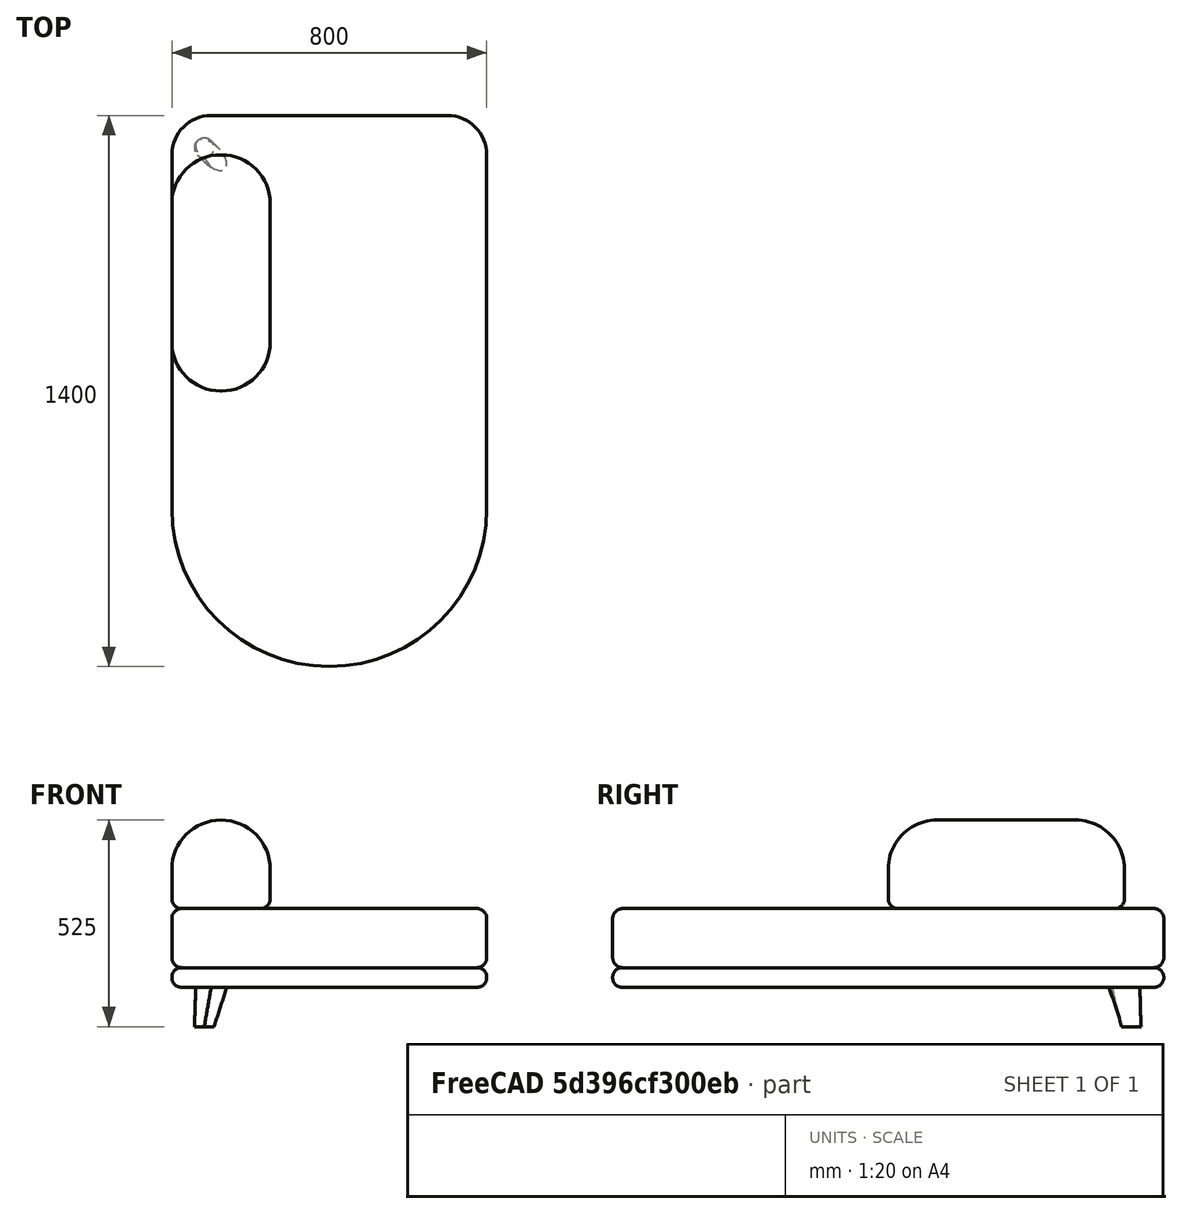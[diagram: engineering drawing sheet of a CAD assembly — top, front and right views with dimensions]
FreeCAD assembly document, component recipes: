
FREECAD ASSEMBLY — COMPONENT RECIPES ("Drawing room Sofa lounger")

This assembly document has 7 components, labeled P0..P6 below (a component is one placed body or linked part). 7 of them carry a construction recipe — the FreeCAD feature program that regenerates the part from scratch, quoted from this document or its linked companion documents; the rest are supplied as boundary geometry only. No exploded tour is included for this assembly.
COMPONENT P0 — recipe-attached ("Backrest001", modeled in this document).
Construction recipe (the document's own serialized feature program — sketch geometry with constraints, then the solid features built on it; lengths are millimeters unless a unit is written):

FEATURE [Sketcher::SketchObject] Sketch002
  ArcFitTolerance = 1e-06
  AttachmentSupport = -> [XZ_Plane002]
  FullyConstrained = true
  MakeInternals = false
  MapMode = 5
  Placement = pos=(0,0,0) rot=(1,0,0;1.5708rad)
  sketch-geometry (5):
    g0: LineSegment StartX=0 StartY=0 StartZ=0 EndX=250 EndY=0 EndZ=0
    g1: LineSegment StartX=250 StartY=0 StartZ=0 EndX=250 EndY=100 EndZ=0
    g2: LineSegment [constr] StartX=250 StartY=100 StartZ=0 EndX=0 EndY=100 EndZ=0
    g3: LineSegment StartX=0 StartY=100 StartZ=0 EndX=0 EndY=0 EndZ=0
    g4: ArcOfCircle CenterX=125 CenterY=100 CenterZ=0 NormalX=0 NormalY=0 NormalZ=1 AngleXU=0 Radius=125 StartAngle=0 EndAngle=3.14159
  constraints (14):
    c: Coincident(g0,g1)
    c: Coincident(g1,g2)
    c: Coincident(g2,g3)
    c: Coincident(g3,g0)
    c: Horizontal(g0)
    c: Horizontal(g2)
    c: Vertical(g1)
    c: Vertical(g3)
    c: Distance(g1,g3) = 250
    c: Distance(g0,g2) = 100
    c: Coincident(g0,g-1)
    c: Coincident(g4,g2)
    c: Coincident(g4,g1)
    c: PointOnObject(g4,g2)
FEATURE [PartDesign::Pad] Pad002
  Direction = (0,-1,2e-16)
  Length = 600
  Length2 = 10
  Placement = pos=(0,0,0) rot=(1,0,0;1.5708rad)
  Profile = -> Sketch002
  ReferenceAxis = -> Sketch002 [N_Axis]
  Refine = true
  Suppressed = false
  Type = 0
FEATURE [PartDesign::Fillet] Fillet002
  Base = -> Pad002 [Edge9,Edge10]
  BaseFeature = -> Pad002
  Placement = pos=(0,0,0) rot=(1,0,0;1.5708rad)
  Radius = 124
  Refine = true
  SupportTransform = false
  Suppressed = false
  UseAllEdges = false
FEATURE [PartDesign::Fillet] Fillet003
  Base = -> Fillet002 [Face1]
  BaseFeature = -> Fillet002
  Placement = pos=(0,0,0) rot=(1,0,0;1.5708rad)
  Radius = 25
  Refine = true
  SupportTransform = false
  Suppressed = false
  UseAllEdges = true
FEATURE [PartDesign::Body] Body002  label="Backrest"
  AllowCompound = false
  Group = -> [Sketch002,Pad002,Fillet002,Fillet003]
  Origin = -> Origin002
  Placement = pos=(0,-100,200) rot=(0,0,1;0rad)
  Tip = -> Fillet003
COMPONENT P1 — recipe-attached ("Base001", modeled in this document).
Construction recipe (the document's own serialized feature program — sketch geometry with constraints, then the solid features built on it; lengths are millimeters unless a unit is written):

FEATURE [Sketcher::SketchObject] Sketch
  ArcFitTolerance = 1e-06
  AttachmentSupport = -> [XY_Plane]
  FullyConstrained = true
  MakeInternals = false
  MapMode = 5
  sketch-geometry (6):
    g0: LineSegment StartX=100 StartY=0 StartZ=0 EndX=700 EndY=0 EndZ=0
    g1: ArcOfCircle CenterX=700 CenterY=-100 CenterZ=0 NormalX=0 NormalY=0 NormalZ=1 AngleXU=0 Radius=100 StartAngle=1e-16 EndAngle=1.5708
    g2: LineSegment StartX=800 StartY=-100 StartZ=0 EndX=800 EndY=-1000 EndZ=0
    g3: ArcOfCircle CenterX=400 CenterY=-1000 CenterZ=0 NormalX=0 NormalY=0 NormalZ=1 AngleXU=0 Radius=400 StartAngle=3.14159 EndAngle=6.28319
    g4: LineSegment StartX=0 StartY=-1000 StartZ=0 EndX=0 EndY=-100 EndZ=0
    g5: ArcOfCircle CenterX=100 CenterY=-100 CenterZ=0 NormalX=0 NormalY=0 NormalZ=1 AngleXU=0 Radius=100 StartAngle=1.5708 EndAngle=3.14159
  constraints (15):
    c: PointOnObject(g0,g-1)
    c: Horizontal(g0)
    c: Tangent(g0,g1) = 1.5708
    c: Tangent(g1,g2) = 1.5708
    c: Tangent(g2,g3) = 1.5708
    c: PointOnObject(g3,g-2)
    c: Tangent(g3,g4) = 1.5708
    c: Tangent(g4,g5) = 1.5708
    c: Radius(g1) = 100
    c: Radius(g5) = 100
    c: Vertical(g4)
    c: Vertical(g2)
    c: Tangent(g5,g0) = 1.5708
    c: DistanceX(g0,g0) = 600
    c: DistanceY(g2,g2) = 900
FEATURE [PartDesign::Pad] Pad
  Direction = (0,0,1)
  Length = 50
  Length2 = 10
  Profile = -> Sketch
  ReferenceAxis = -> Sketch [N_Axis]
  Refine = true
  Suppressed = false
  Type = 0
FEATURE [PartDesign::Fillet] Fillet001
  Base = -> Pad [?Face10]
  BaseFeature = -> Pad
  Radius = 24
  Refine = true
  SupportTransform = false
  Suppressed = false
  UseAllEdges = true
FEATURE [PartDesign::Body] Body  label="Base"
  AllowCompound = false
  Group = -> [Sketch,Pad,Fillet001]
  Origin = -> Origin
  Tip = -> Fillet001
COMPONENT P2 — recipe-attached ("Cushion001", modeled in this document).
Construction recipe (the document's own serialized feature program — sketch geometry with constraints, then the solid features built on it; lengths are millimeters unless a unit is written):

FEATURE [Sketcher::SketchObject] Sketch001
  ArcFitTolerance = 1e-06
  AttachmentSupport = -> [XY_Plane001]
  FullyConstrained = true
  MakeInternals = false
  MapMode = 5
  sketch-geometry (7):
    g0: LineSegment StartX=0 StartY=-100 StartZ=0 EndX=0 EndY=-1000 EndZ=0
    g1: LineSegment StartX=800 StartY=-1000 StartZ=0 EndX=800 EndY=-100 EndZ=0
    g2: LineSegment StartX=700 StartY=0 StartZ=0 EndX=100 EndY=0 EndZ=0
    g3: ArcOfCircle CenterX=100 CenterY=-100 CenterZ=0 NormalX=0 NormalY=0 NormalZ=1 AngleXU=0 Radius=100 StartAngle=1.5708 EndAngle=3.14159
    g4: ArcOfCircle CenterX=700 CenterY=-100 CenterZ=0 NormalX=0 NormalY=0 NormalZ=1 AngleXU=0 Radius=100 StartAngle=0 EndAngle=1.5708
    g5: GeomPoint [constr] X=0 Y=0 Z=0
    g6: ArcOfCircle CenterX=400 CenterY=-1000 CenterZ=0 NormalX=0 NormalY=0 NormalZ=1 AngleXU=0 Radius=400 StartAngle=3.14159 EndAngle=6.28319
  constraints (16):
    c: Tangent(g0,g3) = -1.5708
    c: Tangent(g1,g4) = -1.5708
    c: Tangent(g2,g4) = -1.5708
    c: Tangent(g2,g3) = -1.5708
    c: Vertical(g0)
    c: Vertical(g1)
    c: Horizontal(g2)
    c: PointOnObject(g5,g0)
    c: PointOnObject(g5,g2)
    c: Distance(g0,g1) = 800
    c: Coincident(g5,g-1)
    c: Tangent(g6,g1) = -1.5708
    c: Tangent(g6,g0) = -1.5708
    c: Radius(g4) = 100
    c: Radius(g3) = 100
    c: Distance(g1) = 900
FEATURE [PartDesign::Pad] Pad001
  Direction = (0,0,1)
  Length = 150
  Length2 = 10
  Profile = -> Sketch001
  ReferenceAxis = -> Sketch001 [N_Axis]
  Refine = true
  Suppressed = false
  Type = 0
FEATURE [PartDesign::Fillet] Fillet
  Base = -> Pad001
  BaseFeature = -> Pad001
  Radius = 25
  Refine = true
  SupportTransform = false
  Suppressed = false
  UseAllEdges = true
FEATURE [PartDesign::Body] Body001  label="Cushion"
  AllowCompound = false
  Group = -> [Sketch001,Pad001,Fillet]
  Origin = -> Origin001
  Placement = pos=(0,0,50) rot=(0,0,1;0rad)
  Tip = -> Fillet
COMPONENT P3 — recipe-attached ("Legs001", modeled in this document).
Construction recipe (the document's own serialized feature program — sketch geometry with constraints, then the solid features built on it; lengths are millimeters unless a unit is written):

FEATURE [Sketcher::SketchObject] Sketch003
  ArcFitTolerance = 1e-06
  AttachmentSupport = -> [XY_Plane003]
  FullyConstrained = true
  MakeInternals = false
  MapMode = 5
  sketch-geometry (5):
    g0: Ellipse CenterX=0 CenterY=0 CenterZ=0 NormalX=0 NormalY=0 NormalZ=1 MajorRadius=50 MinorRadius=25 AngleXU=-2.35619
    g1: LineSegment [constr] StartX=-35.3553 StartY=-35.3553 StartZ=0 EndX=35.3553 EndY=35.3553 EndZ=0
    g2: LineSegment [constr] StartX=17.6777 StartY=-17.6777 StartZ=0 EndX=-17.6777 EndY=17.6777 EndZ=0
    g3: GeomPoint [constr] X=-30.6186 Y=-30.6186 Z=0
    g4: GeomPoint [constr] X=30.6186 Y=30.6186 Z=0
  constraints (5):
    c: InternalAlignment(g1-g4 -> g0) x4
    c: Distance(g0,g1) = 50
    c: Angle(g1) = 0.785398
    c: Distance(g0,g2) = 25
    c: Coincident(g0,g-1)
FEATURE [PartDesign::Plane] DatumPlane
  AttachmentOffset = pos=(0,0,-100) rot=(0,0,1;0rad)
  AttachmentSupport = -> [Sketch003]
  Length = 98.636
  MapMode = 2
  Placement = pos=(0,0,-100) rot=(0,0,1;0rad)
  ResizeMode = 0
  Width = 98.6418
FEATURE [Sketcher::SketchObject] Sketch004
  ArcFitTolerance = 1e-06
  AttachmentSupport = -> [DatumPlane]
  FullyConstrained = true
  MakeInternals = false
  MapMode = 5
  Placement = pos=(0,0,-100) rot=(0,0,1;0rad)
  sketch-geometry (2):
    g0: Circle CenterX=-17.6777 CenterY=-17.6777 CenterZ=0 NormalX=0 NormalY=0 NormalZ=1 AngleXU=0 Radius=25
    g1: LineSegment [constr] StartX=-17.6777 StartY=-17.6777 StartZ=0 EndX=2.4e-15 EndY=4.5e-15 EndZ=0
  constraints (5):
    c: Diameter(g0) = 50
    c: Coincident(g1,g0)
    c: Coincident(g1,g-1)
    c: Angle(g1,g-1) = 2.35619
    c: PointOnObject(g1,g0)
FEATURE [PartDesign::AdditiveLoft] AdditiveLoft
  Closed = false
  Profile = -> Sketch003
  Refine = true
  Ruled = false
  Sections = -> [Sketch004]
  Suppressed = false
FEATURE [PartDesign::Body] Body003  label="Legs"
  AllowCompound = false
  Group = -> [Sketch003,DatumPlane,Sketch004,AdditiveLoft]
  Origin = -> Origin003
  Placement = pos=(100,-100,0) rot=(0,0,1;-1.5708rad)
  Tip = -> AdditiveLoft
COMPONENT P4 — same part as P3; its construction recipe is shown at P3.
COMPONENT P5 — same part as P3; its construction recipe is shown at P3.
COMPONENT P6 — same part as P3; its construction recipe is shown at P3.
PROVENANCE & LICENSES
A FreeCAD (.FCStd) document from a public repository crawl; recipes are the document's own serialized feature recipes (and, for linked parts, companion documents' recipes).
License: as declared in the source repository (recorded in the dataset sidecar).
